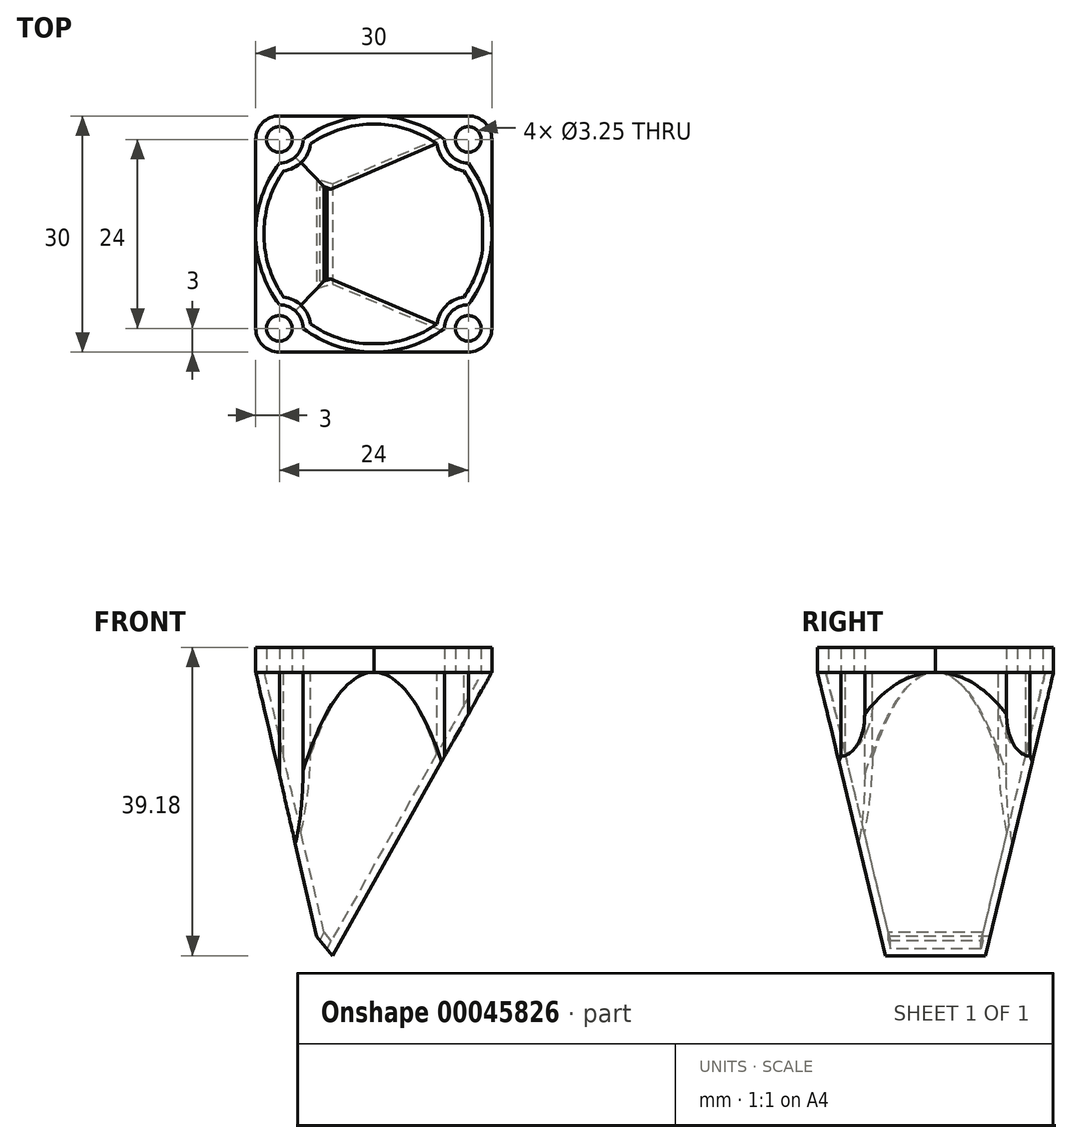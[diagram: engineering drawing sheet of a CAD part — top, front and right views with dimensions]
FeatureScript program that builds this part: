
annotation { "Feature Type Name" : "Feature", "Feature Type Description" : "" }
export const myFeature = defineFeature(function(context is Context, id is Id, definition is map)
    precondition{}
    {
        {
            var Q0;
            Q0=qCreatedBy(makeId("Top.planeOp"),FACE);
            var sketch = newSketch(context, id + "F0", { "sketchPlane" : qUnion([Q0])});
            skCircle(sketch, "E0", {"center": v(0, 15) * mm, "radius": 15 * mm});
            skLineSegment(sketch, "E1", {"start": v(0, 0) * mm, "end": v(0, 15) * mm, "construction": true});
            skSolve(sketch);
        }
        {
            var Q0;
            Q0=qSketchRegion(id+"F0",true);
            extrude(context, id + "F1", {"entities" : qUnion([Q0]), "oppositeDirection" : true, "depth" : 50.8 * mm});
        }
        {
            var Q0;
            Q0=qCreatedBy(makeId("Front.planeOp"),FACE);
            var sketch = newSketch(context, id + "F2", { "sketchPlane" : qUnion([Q0])});
            skPoint(sketch, "E2", {"position": v(0, 0) * mm});
            skLineSegment(sketch, "E3.top", {"start": v(-15, -50.8) * mm, "end": v(15, -50.8) * mm});
            skLineSegment(sketch, "E3.left", {"start": v(-15, 0) * mm, "end": v(-15, -50.8) * mm});
            skLineSegment(sketch, "E3.right", {"start": v(15, 0) * mm, "end": v(15, -50.8) * mm});
            skLineSegment(sketch, "E4", {"start": v(15, 0) * mm, "end": v(-5.26, -36) * mm});
            skPoint(sketch, "E5.endSnap0", {"position": v(-6.26, -34.77) * mm});
            skLineSegment(sketch, "E6", {"start": v(-15, 0) * mm, "end": v(-7.26, -33.53) * mm});
            skLineSegment(sketch, "E7", {"start": v(15, 0) * mm, "end": v(-15, 0) * mm, "construction": true});
            skLineSegment(sketch, "E8", {"start": v(-5.26, -36) * mm, "end": v(-7.26, -33.53) * mm});
            skSolve(sketch);
        }
        {
            var Q0;
            Q0=qSketchRegion(id+"F2",true);
            var Q1;
            Q1=makeQuery(id+"F1.opExtrude","SWEPT_FACE",FACE,{"disambiguationData":[OSD([sQuery(id+"F0.wireOp",EDGE,"E0")])]});
            extrude(context, id + "F3", {"entities" : qUnion([Q0]), "operationType" : NewBodyOperationType.REMOVE, "oppositeDirection" : true, "endBoundEntityFace" : qUnion([Q1]), "depth" : 50.8 * mm});
        }
        {
            var Q0;
            Q0=qCreatedBy(makeId("Right.planeOp"),FACE);
            var sketch = newSketch(context, id + "F4", { "sketchPlane" : qUnion([Q0])});
            skLineSegment(sketch, "E9.bottom", {"start": v(30, 0) * mm, "end": v(0, 0) * mm, "construction": true});
            skLineSegment(sketch, "E9.left", {"start": v(30, 0) * mm, "end": v(30, -36) * mm});
            skLineSegment(sketch, "E9.right", {"start": v(0, 0) * mm, "end": v(0, -36) * mm});
            skPoint(sketch, "E10", {"position": v(15, 0) * mm});
            skLineSegment(sketch, "E11", {"start": v(0, -36) * mm, "end": v(8.65, -36) * mm});
            skLineSegment(sketch, "E12", {"start": v(8.65, -36) * mm, "end": v(21.35, -36) * mm, "construction": true});
            skLineSegment(sketch, "E13", {"start": v(21.35, -36) * mm, "end": v(30, -36) * mm});
            skLineSegment(sketch, "E14", {"start": v(0, 0) * mm, "end": v(8.65, -36) * mm});
            skLineSegment(sketch, "E15", {"start": v(21.35, -36) * mm, "end": v(30, 0) * mm});
            skSolve(sketch);
        }
        {
            var Q0;
            Q0=qSketchRegion(id+"F4",true);
            var Q1;
            Q1=makeQuery(id+"F1.opExtrude","SWEPT_FACE",FACE,{"disambiguationData":[OSD([sQuery(id+"F0.wireOp",EDGE,"E0")])]});
            extrude(context, id + "F5", {"entities" : qUnion([Q0]), "operationType" : NewBodyOperationType.REMOVE, "endBound" : BoundingType.UP_TO_SURFACE, "oppositeDirection" : true, "endBoundEntityFace" : qUnion([Q1]), "depth" : 25.4 * mm, "hasSecondDirection" : true, "secondDirectionOppositeDirection" : false, "secondDirectionDepth" : 25.4 * mm});
        }
        {
            var Q0;
            Q0=makeQuery(id+"F1.opExtrude","CAP_FACE",FACE,{"disambiguationData":[OSD([sQuery(id+"F0.wireOp",EDGE,"E0")])],"isStart":true});
            var sketch = newSketch(context, id + "F6", { "sketchPlane" : qUnion([Q0])});
            skLineSegment(sketch, "E16.rect.bottom", {"start": v(15, 0) * mm, "end": v(-15, 0) * mm, "construction": true});
            skLineSegment(sketch, "E16.rect.top", {"start": v(15, 30) * mm, "end": v(-15, 30) * mm, "construction": true});
            skLineSegment(sketch, "E16.rect.left", {"start": v(15, 0) * mm, "end": v(15, 30) * mm, "construction": true});
            skLineSegment(sketch, "E16.rect.right", {"start": v(-15, 0) * mm, "end": v(-15, 30) * mm, "construction": true});
            skPoint(sketch, "E16.rect.middle", {"position": v(0, 15) * mm});
            skCircle(sketch, "E17", {"center": v(12, 27) * mm, "radius": 3 * mm});
            skLineSegment(sketch, "E18.rect.bottom", {"start": v(12, 27) * mm, "end": v(-12, 27) * mm, "construction": true});
            skLineSegment(sketch, "E18.rect.top", {"start": v(12, 3) * mm, "end": v(-12, 3) * mm, "construction": true});
            skLineSegment(sketch, "E18.rect.left", {"start": v(12, 27) * mm, "end": v(12, 3) * mm, "construction": true});
            skLineSegment(sketch, "E18.rect.right", {"start": v(-12, 27) * mm, "end": v(-12, 3) * mm, "construction": true});
            skCircle(sketch, "E19", {"center": v(12, 3) * mm, "radius": 3 * mm});
            skCircle(sketch, "E20", {"center": v(-12, 3) * mm, "radius": 3 * mm});
            skCircle(sketch, "E21", {"center": v(-12, 27) * mm, "radius": 3 * mm});
            skSolve(sketch);
        }
        {
            var Q0;
            Q0=qSketchRegion(id+"F6",true);
            var Q1;
            Q1=makeQuery(id+"F3.boolean.opBoolean","COPY",FACE,{"derivedFrom":makeQuery(id+"F3.opExtrude","SWEPT_FACE",FACE,{"disambiguationData":[OSD([sQuery(id+"F2.wireOp",EDGE,"E4")])]})});
            extrude(context, id + "F7", {"entities" : qUnion([Q0]), "operationType" : NewBodyOperationType.REMOVE, "endBound" : BoundingType.UP_TO_SURFACE, "oppositeDirection" : true, "endBoundEntityFace" : qUnion([Q1]), "depth" : 25.4 * mm});
        }
        {
            var Q0;
            Q0=makeQuery(id+"F1.opExtrude","CAP_FACE",FACE,{"disambiguationData":[OSD([sQuery(id+"F0.wireOp",EDGE,"E0")])],"isStart":true});
            shell(context, id + "F8", {"entities" : qUnion([Q0]), "thickness" : 1.03 * mm});
        }
        {
            var Q0;
            Q0=makeQuery(id+"F1.opExtrude","CAP_FACE",FACE,{"disambiguationData":[OSD([sQuery(id+"F0.wireOp",EDGE,"E0")])],"isStart":true});
            var sketch = newSketch(context, id + "F9", { "sketchPlane" : qUnion([Q0])});
            skLineSegment(sketch, "E22.rect.bottom", {"start": v(15, 0) * mm, "end": v(-15, 0) * mm});
            skLineSegment(sketch, "E22.rect.top", {"start": v(15, 30) * mm, "end": v(-15, 30) * mm});
            skLineSegment(sketch, "E22.rect.left", {"start": v(15, 0) * mm, "end": v(15, 30) * mm});
            skLineSegment(sketch, "E22.rect.right", {"start": v(-15, 0) * mm, "end": v(-15, 30) * mm});
            skPoint(sketch, "E22.rect.middle", {"position": v(0, 15) * mm});
            skCircle(sketch, "E23", {"center": v(12, 27) * mm, "radius": 1.63 * mm});
            skCircle(sketch, "E24", {"center": v(12, 3) * mm, "radius": 1.63 * mm});
            skCircle(sketch, "E25", {"center": v(-12, 3) * mm, "radius": 1.63 * mm});
            skCircle(sketch, "E26", {"center": v(-12, 27) * mm, "radius": 1.63 * mm});
            skSolve(sketch);
        }
        {
            var Q0;
            Q0=makeQuery(id+"F9.imprint","IMPRINT",FACE,{"disambiguationData":[TD([[makeQuery(id+"F9.imprint","IMPRINT",EDGE,{"derivedFrom":sQuery(id+"F9.wireOp",EDGE,"E24")}),-1.0]])]});
            var Q1;
            Q1=makeQuery(id+"F9.imprint","IMPRINT",FACE,{"disambiguationData":[TD([[makeQuery(id+"F9.imprint","IMPRINT",EDGE,{"derivedFrom":sQuery(id+"F9.wireOp",EDGE,"E25")}),-1.0]])]});
            var Q2;
            Q2=makeQuery(id+"F9.imprint","IMPRINT",FACE,{"disambiguationData":[TD([[makeQuery(id+"F9.imprint","IMPRINT",EDGE,{"derivedFrom":sQuery(id+"F9.wireOp",EDGE,"E23")}),-1.0]])]});
            var Q3;
            Q3=makeQuery(id+"F9.imprint","IMPRINT",FACE,{"disambiguationData":[TD([[makeQuery(id+"F9.imprint","IMPRINT",EDGE,{"derivedFrom":sQuery(id+"F9.wireOp",EDGE,"E26")}),-1.0]])]});
            var Q4;
            {var subQ18=sQuery(id+"F6.wireOp",EDGE,"E17");var subQ30=makeQuery(id+"F7.boolean.opBoolean","COPY",EDGE,{"derivedFrom":makeQuery(id+"F7.opExtrude","CAP_EDGE",EDGE,{"disambiguationData":[OSD([subQ18])],"isStart":true})});Q4=makeQuery(id+"F9.imprint","IMPRINT",FACE,{"disambiguationData":[TD([[makeQuery(id+"F9.imprint","IMPRINT",EDGE,{"derivedFrom":subQ30}),-1.0]])]});}
            extrude(context, id + "F10", {"entities" : qUnion([Q0, Q1, Q2, Q3, Q4]), "operationType" : NewBodyOperationType.ADD, "depth" : 3.17 * mm});
        }
        {
            var Q0;
            Q0=makeQuery(id+"F10.opExtrude","SWEPT_EDGE",EDGE,{"disambiguationData":[OSD([sQuery(id+"F9.wireOp",EDGE,"E22.rect.bottom"),sQuery(id+"F9.wireOp",EDGE,"E22.rect.left")])]});
            var Q1;
            Q1=makeQuery(id+"F10.opExtrude","SWEPT_EDGE",EDGE,{"disambiguationData":[OSD([sQuery(id+"F9.wireOp",EDGE,"E22.rect.bottom"),sQuery(id+"F9.wireOp",EDGE,"E22.rect.right")])]});
            var Q2;
            Q2=makeQuery(id+"F10.opExtrude","SWEPT_EDGE",EDGE,{"disambiguationData":[OSD([sQuery(id+"F9.wireOp",EDGE,"E22.rect.top"),sQuery(id+"F9.wireOp",EDGE,"E22.rect.right")])]});
            var Q3;
            Q3=makeQuery(id+"F10.opExtrude","SWEPT_EDGE",EDGE,{"disambiguationData":[OSD([sQuery(id+"F9.wireOp",EDGE,"E22.rect.top"),sQuery(id+"F9.wireOp",EDGE,"E22.rect.left")])]});
            fillet(context, id + "F11", {"entities" : qUnion([Q0, Q1, Q2, Q3]), "radius" : 3 * mm, "tangentPropagation" : true, "allowEdgeOverflow" : false});
        }
        {
            var Q0;
            Q0=makeQuery(id+"F3.boolean.opBoolean","COPY",FACE,{"derivedFrom":makeQuery(id+"F3.opExtrude","SWEPT_FACE",FACE,{"disambiguationData":[OSD([sQuery(id+"F2.wireOp",EDGE,"E4")])]})});
            var sketch = newSketch(context, id + "F12", { "sketchPlane" : qUnion([Q0])});
            skLineSegment(sketch, "E27.bottom", {"start": v(8.22, -11.3) * mm, "end": v(20.63, -11.3) * mm});
            skLineSegment(sketch, "E27.top", {"start": v(8.22, -13.02) * mm, "end": v(20.63, -13.02) * mm});
            skLineSegment(sketch, "E27.left", {"start": v(8.22, -11.3) * mm, "end": v(8.22, -13.02) * mm});
            skLineSegment(sketch, "E27.right", {"start": v(20.63, -11.3) * mm, "end": v(20.63, -13.02) * mm});
            skSolve(sketch);
        }
        {
            var Q0;
            Q0=qSketchRegion(id+"F12",true);
            var Q1;
            Q1=makeQuery(id+"F8.opShell","OFFSET_FACE",FACE,{"disambiguationData":[OSD([sQuery(id+"F2.wireOp",EDGE,"E4")])]});
            extrude(context, id + "F13", {"entities" : qUnion([Q0]), "operationType" : NewBodyOperationType.REMOVE, "endBound" : BoundingType.UP_TO_SURFACE, "oppositeDirection" : true, "endBoundEntityFace" : qUnion([Q1]), "depth" : 25.4 * mm});
        }
        {
            var Q0;
            Q0=makeQuery(id+"F13.boolean.opBoolean","COPY",FACE,{"derivedFrom":makeQuery(id+"F13.opExtrude","SWEPT_FACE",FACE,{"disambiguationData":[OSD([sQuery(id+"F12.wireOp",EDGE,"E27.top")])]})});
            var sketch = newSketch(context, id + "F14", { "sketchPlane" : qUnion([Q0])});
            skLineSegment(sketch, "E28", {"start": v(12.04, 20.73) * mm, "end": v(10.72, 21) * mm});
            skLineSegment(sketch, "E29", {"start": v(12.04, 9.27) * mm, "end": v(10.72, 9) * mm});
            skLineSegment(sketch, "E30", {"start": v(10.72, 21) * mm, "end": v(10.72, 9) * mm});
            skLineSegment(sketch, "E31", {"start": v(12.04, 20.73) * mm, "end": v(12.04, 9.27) * mm});
            skSolve(sketch);
        }
        {
            var Q0;
            Q0=qSketchRegion(id+"F14",true);
            var Q1;
            Q1=makeQuery(id+"F3.boolean.opBoolean","COPY",FACE,{"derivedFrom":makeQuery(id+"F3.opExtrude","SWEPT_FACE",FACE,{"disambiguationData":[OSD([sQuery(id+"F2.wireOp",EDGE,"E8")])]})});
            extrude(context, id + "F15", {"entities" : qUnion([Q0]), "operationType" : NewBodyOperationType.REMOVE, "endBound" : BoundingType.UP_TO_SURFACE, "oppositeDirection" : true, "endBoundEntityFace" : qUnion([Q1]), "depth" : 25.4 * mm});
        }
        {
            var Q0;
            Q0=makeQuery(id+"F13.boolean.opBoolean","COPY",FACE,{"derivedFrom":makeQuery(id+"F13.opExtrude","SWEPT_FACE",FACE,{"disambiguationData":[OSD([sQuery(id+"F12.wireOp",EDGE,"E27.top")])]})});
            var Q1;
            Q1=makeQuery(id+"F13.boolean.opBoolean","COPY",FACE,{"derivedFrom":makeQuery(id+"F13.opExtrude","SWEPT_FACE",FACE,{"disambiguationData":[OSD([sQuery(id+"F12.wireOp",EDGE,"E27.bottom")])]})});
            extrude(context, id + "F16", {"entities" : qUnion([Q0]), "operationType" : NewBodyOperationType.ADD, "endBound" : BoundingType.UP_TO_SURFACE, "endBoundEntityFace" : qUnion([Q1]), "depth" : 25.4 * mm});
        }
    });
